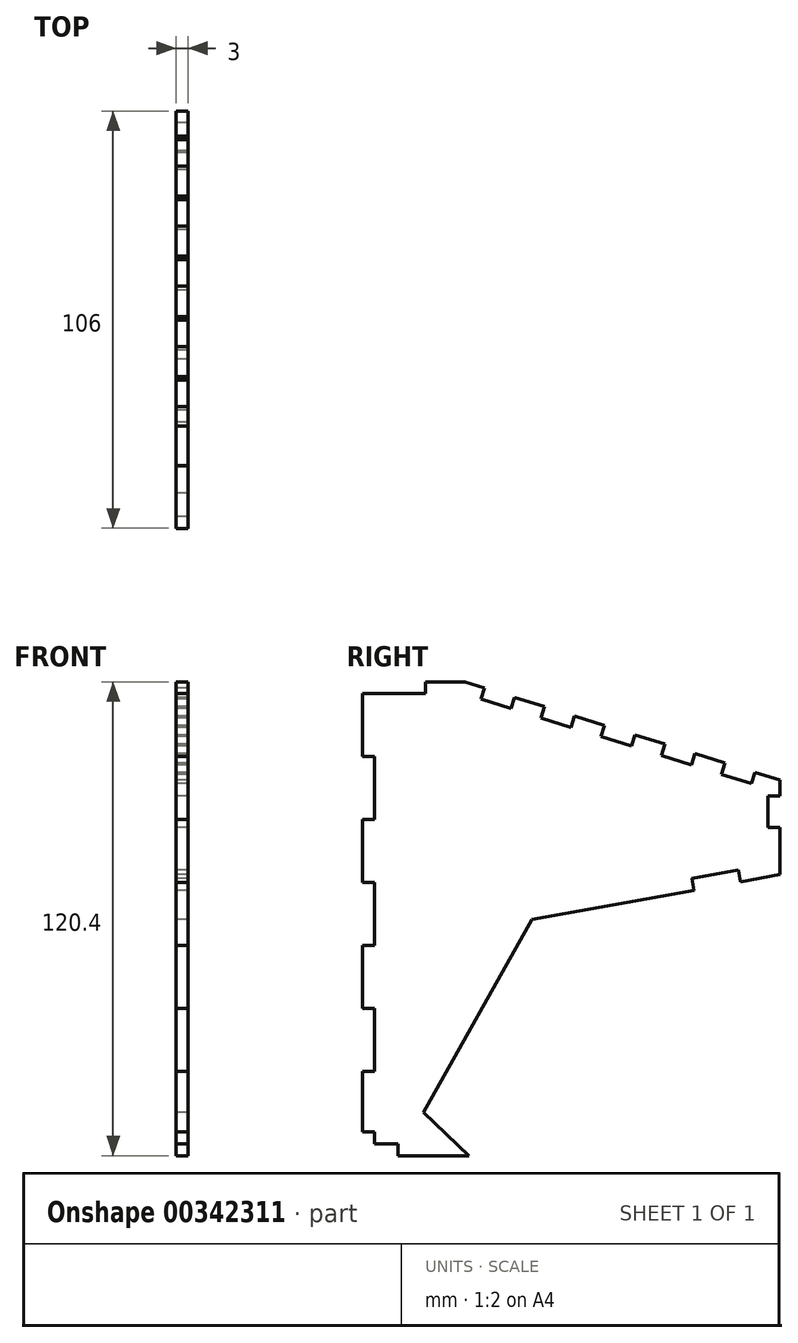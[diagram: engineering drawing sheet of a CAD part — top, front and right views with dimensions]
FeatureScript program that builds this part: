
annotation { "Feature Type Name" : "Feature", "Feature Type Description" : "" }
export const myFeature = defineFeature(function(context is Context, id is Id, definition is map)
    precondition{}
    {
        {
            var Q0;
            Q0=qCreatedBy(makeId("Right.planeOp"),FACE);
            var sketch = newSketch(context, id + "F0", { "sketchPlane" : qUnion([Q0])});
            skLineSegment(sketch, "E0.top", {"start": v(-28.67, -48.45) * mm, "end": v(-10.67, -48.45) * mm});
            skLineSegment(sketch, "E1", {"start": v(68.33, 22.95) * mm, "end": v(5.33, 11.55) * mm, "construction": true});
            skLineSegment(sketch, "E2", {"start": v(-37.67, 71.95) * mm, "end": v(-21.67, 71.95) * mm, "construction": true});
            skLineSegment(sketch, "E3", {"start": v(-21.67, 71.95) * mm, "end": v(-11.67, 71.95) * mm});
            skLineSegment(sketch, "E4", {"start": v(-21.67, 71.95) * mm, "end": v(-21.67, 68.95) * mm});
            skLineSegment(sketch, "E5", {"start": v(-21.67, 68.95) * mm, "end": v(-37.67, 68.95) * mm});
            skLineSegment(sketch, "E6", {"start": v(-37.67, 68.95) * mm, "end": v(-37.67, 52.95) * mm});
            skLineSegment(sketch, "E7", {"start": v(-37.67, 52.95) * mm, "end": v(-34.67, 52.95) * mm});
            skLineSegment(sketch, "E8", {"start": v(-34.67, 52.95) * mm, "end": v(-34.67, 36.95) * mm});
            skLineSegment(sketch, "E9", {"start": v(-34.67, 36.95) * mm, "end": v(-37.67, 36.95) * mm});
            skLineSegment(sketch, "E10", {"start": v(-37.67, 36.95) * mm, "end": v(-37.67, 20.95) * mm});
            skLineSegment(sketch, "E11", {"start": v(-37.67, 20.95) * mm, "end": v(-34.67, 20.95) * mm});
            skLineSegment(sketch, "E12", {"start": v(-34.67, 20.95) * mm, "end": v(-34.67, 4.95) * mm});
            skLineSegment(sketch, "E13", {"start": v(-34.67, 4.95) * mm, "end": v(-37.67, 4.95) * mm});
            skLineSegment(sketch, "E14", {"start": v(-37.67, 4.95) * mm, "end": v(-37.67, -11.05) * mm});
            skLineSegment(sketch, "E15", {"start": v(-37.67, -11.05) * mm, "end": v(-34.67, -11.05) * mm});
            skLineSegment(sketch, "E16", {"start": v(-34.67, -11.05) * mm, "end": v(-34.67, -27.05) * mm});
            skLineSegment(sketch, "E17", {"start": v(-34.67, -27.05) * mm, "end": v(-37.67, -27.05) * mm});
            skLineSegment(sketch, "E18", {"start": v(-37.67, -37.45) * mm, "end": v(-22.17, -37.45) * mm, "construction": true});
            skLineSegment(sketch, "E19", {"start": v(-22.17, -37.45) * mm, "end": v(-10.67, -48.45) * mm});
            skLineSegment(sketch, "E20", {"start": v(5.33, 11.55) * mm, "end": v(-22.17, -37.45) * mm});
            skLineSegment(sketch, "E21", {"start": v(68.33, 46.95) * mm, "end": v(68.33, 42.95) * mm});
            skLineSegment(sketch, "E22", {"start": v(68.33, 42.95) * mm, "end": v(65.33, 42.95) * mm});
            skLineSegment(sketch, "E23", {"start": v(65.33, 42.95) * mm, "end": v(65.33, 34.95) * mm});
            skLineSegment(sketch, "E24", {"start": v(65.33, 34.95) * mm, "end": v(68.33, 34.95) * mm});
            skLineSegment(sketch, "E25", {"start": v(68.33, 34.95) * mm, "end": v(68.33, 22.95) * mm});
            skLineSegment(sketch, "E26", {"start": v(-37.67, -27.05) * mm, "end": v(-37.67, -42.45) * mm});
            skLineSegment(sketch, "E27", {"start": v(-37.67, -42.45) * mm, "end": v(-34.67, -42.45) * mm});
            skLineSegment(sketch, "E28", {"start": v(-34.67, -42.45) * mm, "end": v(-34.67, -45.45) * mm});
            skLineSegment(sketch, "E29", {"start": v(-34.67, -45.45) * mm, "end": v(-28.67, -45.45) * mm});
            skLineSegment(sketch, "E30", {"start": v(-28.67, -45.45) * mm, "end": v(-28.67, -48.45) * mm});
            skLineSegment(sketch, "E31", {"start": v(-11.67, 71.95) * mm, "end": v(23.8, 60.86) * mm, "construction": true});
            skLineSegment(sketch, "E32", {"start": v(23.8, 60.86) * mm, "end": v(22.9, 58) * mm});
            skLineSegment(sketch, "E33", {"start": v(45.82, 50.84) * mm, "end": v(46.71, 53.7) * mm});
            skLineSegment(sketch, "E34", {"start": v(46.71, 53.7) * mm, "end": v(68.33, 46.95) * mm, "construction": true});
            skLineSegment(sketch, "E35", {"start": v(22.9, 58) * mm, "end": v(30.54, 55.61) * mm});
            skLineSegment(sketch, "E36", {"start": v(30.54, 55.61) * mm, "end": v(31.44, 58.47) * mm});
            skLineSegment(sketch, "E37", {"start": v(31.44, 58.47) * mm, "end": v(39.07, 56.09) * mm});
            skLineSegment(sketch, "E38", {"start": v(39.07, 56.09) * mm, "end": v(38.18, 53.22) * mm});
            skLineSegment(sketch, "E39", {"start": v(38.18, 53.22) * mm, "end": v(45.82, 50.84) * mm});
            skLineSegment(sketch, "E40", {"start": v(46.52, 19) * mm, "end": v(45.98, 21.95) * mm});
            skLineSegment(sketch, "E41", {"start": v(45.98, 21.95) * mm, "end": v(57.8, 24.09) * mm});
            skLineSegment(sketch, "E42", {"start": v(57.8, 24.09) * mm, "end": v(58.33, 21.14) * mm});
            skLineSegment(sketch, "E43", {"start": v(46.52, 19) * mm, "end": v(5.33, 11.55) * mm});
            skLineSegment(sketch, "E44", {"start": v(58.33, 21.14) * mm, "end": v(68.33, 22.95) * mm});
            skLineSegment(sketch, "E45", {"start": v(23.8, 60.86) * mm, "end": v(16.17, 63.25) * mm});
            skLineSegment(sketch, "E46", {"start": v(16.17, 63.25) * mm, "end": v(15.27, 60.38) * mm});
            skLineSegment(sketch, "E47", {"start": v(15.27, 60.38) * mm, "end": v(7.64, 62.77) * mm});
            skLineSegment(sketch, "E48", {"start": v(7.64, 62.77) * mm, "end": v(8.53, 65.63) * mm});
            skLineSegment(sketch, "E49", {"start": v(8.53, 65.63) * mm, "end": v(0.9, 68.02) * mm});
            skLineSegment(sketch, "E50", {"start": v(0.9, 68.02) * mm, "end": v(0, 65.16) * mm});
            skLineSegment(sketch, "E51", {"start": v(0, 65.16) * mm, "end": v(-7.64, 67.54) * mm});
            skLineSegment(sketch, "E52", {"start": v(-7.64, 67.54) * mm, "end": v(-6.74, 70.4) * mm});
            skLineSegment(sketch, "E53", {"start": v(-6.74, 70.4) * mm, "end": v(-11.67, 71.95) * mm});
            skLineSegment(sketch, "E54", {"start": v(46.71, 53.7) * mm, "end": v(54.35, 51.32) * mm});
            skLineSegment(sketch, "E55", {"start": v(54.35, 51.32) * mm, "end": v(53.45, 48.45) * mm});
            skLineSegment(sketch, "E56", {"start": v(53.45, 48.45) * mm, "end": v(61.09, 46.07) * mm});
            skLineSegment(sketch, "E57", {"start": v(61.09, 46.07) * mm, "end": v(61.98, 48.93) * mm});
            skLineSegment(sketch, "E58", {"start": v(61.98, 48.93) * mm, "end": v(68.33, 46.95) * mm});
            skSolve(sketch);
        }
        {
            var Q0;
            Q0=qSketchRegion(id+"F0",true);
            extrude(context, id + "F1", {"entities" : qUnion([Q0]), "offsetDistance" : 25 * mm, "depth" : 3 * mm});
        }
    });
